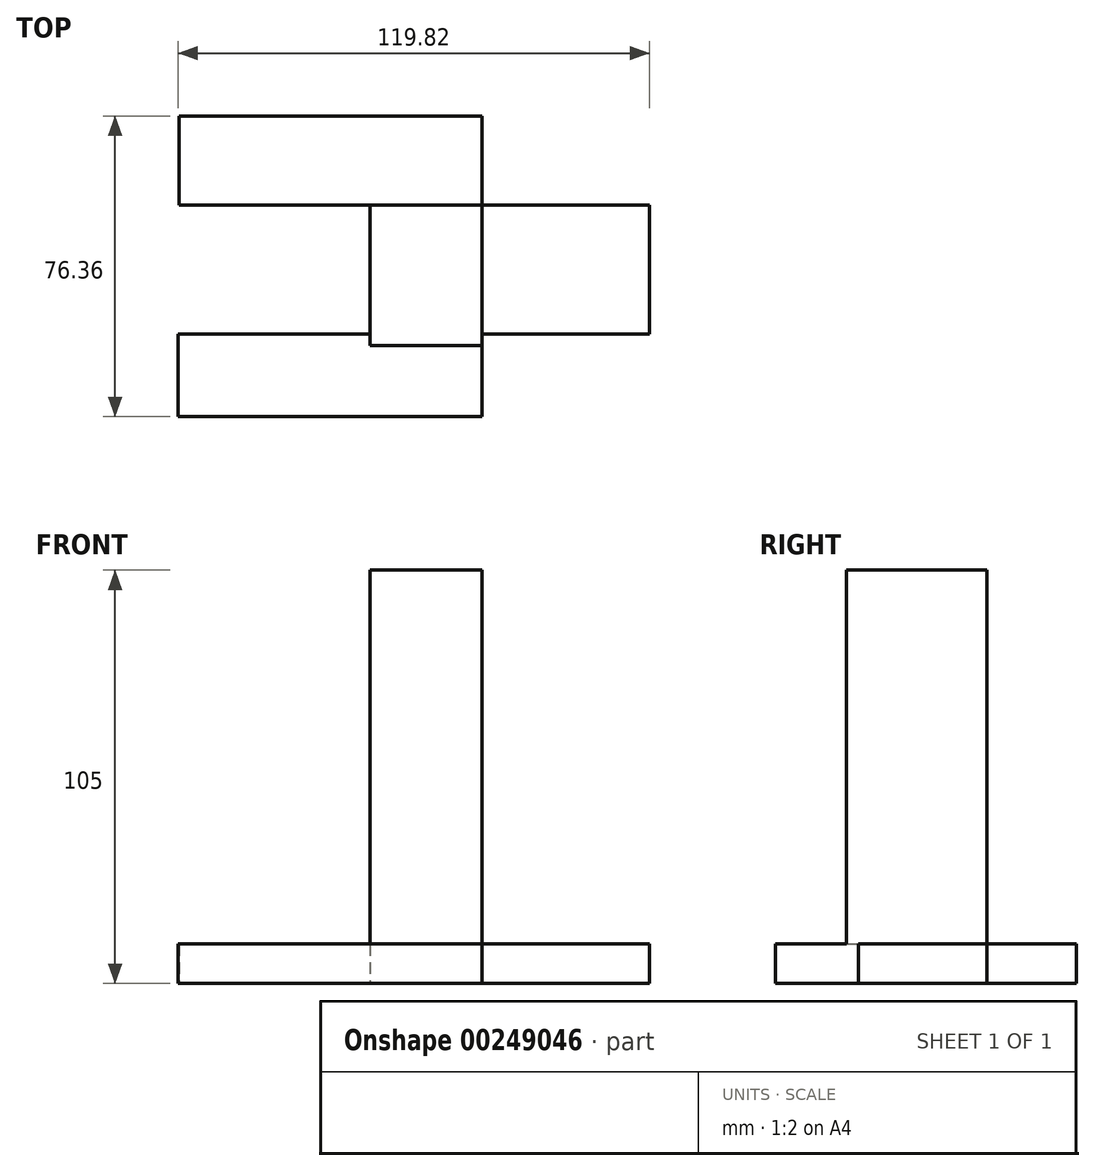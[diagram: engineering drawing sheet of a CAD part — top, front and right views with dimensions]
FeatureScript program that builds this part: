
annotation { "Feature Type Name" : "Feature", "Feature Type Description" : "" }
export const myFeature = defineFeature(function(context is Context, id is Id, definition is map)
    precondition{}
    {
        {
            var Q0;
            Q0=qCreatedBy(makeId("Top.planeOp"),FACE);
            var sketch = newSketch(context, id + "F0", { "sketchPlane" : qUnion([Q0])});
            skLineSegment(sketch, "E0", {"start": v(-59.64, 36.02) * mm, "end": v(17.27, 36.02) * mm});
            skLineSegment(sketch, "E1", {"start": v(17.27, 36.02) * mm, "end": v(17.27, 13.36) * mm});
            skLineSegment(sketch, "E2", {"start": v(17.27, 13.36) * mm, "end": v(59.9, 13.36) * mm});
            skLineSegment(sketch, "E3", {"start": v(59.9, 13.36) * mm, "end": v(59.9, -19.3) * mm});
            skLineSegment(sketch, "E4", {"start": v(59.9, -19.3) * mm, "end": v(17.27, -19.3) * mm});
            skLineSegment(sketch, "E5", {"start": v(17.27, -19.3) * mm, "end": v(17.27, -40.34) * mm});
            skLineSegment(sketch, "E6", {"start": v(17.27, -40.34) * mm, "end": v(-59.9, -40.34) * mm});
            skLineSegment(sketch, "E7", {"start": v(-59.9, -40.34) * mm, "end": v(-59.9, -19.3) * mm});
            skLineSegment(sketch, "E8", {"start": v(-59.9, -19.3) * mm, "end": v(-26.18, -19.3) * mm});
            skLineSegment(sketch, "E9", {"start": v(-26.18, -19.3) * mm, "end": v(-26.18, 13.36) * mm});
            skLineSegment(sketch, "E10", {"start": v(-26.18, 13.36) * mm, "end": v(-59.64, 13.36) * mm});
            skLineSegment(sketch, "E11", {"start": v(-59.64, 13.36) * mm, "end": v(-59.64, 36.02) * mm});
            skSolve(sketch);
        }
        {
            var Q0;
            Q0=makeQuery(id+"F0.imprint","IMPRINT",FACE,{"disambiguationData":[TD([[makeQuery(id+"F0.imprint","IMPRINT",EDGE,{"derivedFrom":sQuery(id+"F0.wireOp",EDGE,"E0")}),-1.0]])]});
            extrude(context, id + "F1", {"entities" : qUnion([Q0]), "depth" : 10 * mm});
        }
        {
            var Q0;
            Q0=makeQuery(id+"F1.opExtrude","SWEPT_FACE",FACE,{"disambiguationData":[OSD([sQuery(id+"F0.wireOp",EDGE,"E9")])]});
            extrude(context, id + "F2", {"entities" : qUnion([Q0]), "operationType" : NewBodyOperationType.REMOVE, "oppositeDirection" : true, "depth" : 15 * mm});
        }
        {
            var Q0;
            Q0=makeQuery(id+"F1.opExtrude","CAP_FACE",FACE,{"disambiguationData":[OSD([sQuery(id+"F0.wireOp",EDGE,"E0"),sQuery(id+"F0.wireOp",EDGE,"E1"),sQuery(id+"F0.wireOp",EDGE,"E2"),sQuery(id+"F0.wireOp",EDGE,"E3"),sQuery(id+"F0.wireOp",EDGE,"E4"),sQuery(id+"F0.wireOp",EDGE,"E5"),sQuery(id+"F0.wireOp",EDGE,"E6"),sQuery(id+"F0.wireOp",EDGE,"E7"),sQuery(id+"F0.wireOp",EDGE,"E8"),sQuery(id+"F0.wireOp",EDGE,"E9"),sQuery(id+"F0.wireOp",EDGE,"E10"),sQuery(id+"F0.wireOp",EDGE,"E11")])],"isStart":false});
            var sketch = newSketch(context, id + "F3", { "sketchPlane" : qUnion([Q0])});
            skLineSegment(sketch, "E12.bottom", {"start": v(-11.18, 13.36) * mm, "end": v(17.27, 13.36) * mm});
            skLineSegment(sketch, "E12.top", {"start": v(-11.18, -19.3) * mm, "end": v(17.27, -19.3) * mm});
            skLineSegment(sketch, "E12.left", {"start": v(-11.18, 13.36) * mm, "end": v(-11.18, -19.3) * mm});
            skLineSegment(sketch, "E12.right", {"start": v(17.27, 13.36) * mm, "end": v(17.27, -19.3) * mm});
            skSolve(sketch);
        }
        {
            var Q0;
            Q0=makeQuery(id+"F3.imprint","IMPRINT",FACE,{"disambiguationData":[TD([[makeQuery(id+"F3.imprint","IMPRINT",EDGE,{"derivedFrom":sQuery(id+"F3.wireOp",EDGE,"E12.bottom")}),-1.0]])]});
            extrude(context, id + "F4", {"entities" : qUnion([Q0]), "operationType" : NewBodyOperationType.ADD, "depth" : 50 * mm});
        }
        {
            var Q0;
            Q0=makeQuery(id+"F4.opExtrude","CAP_FACE",FACE,{"disambiguationData":[OSD([sQuery(id+"F3.wireOp",EDGE,"E12.bottom"),sQuery(id+"F3.wireOp",EDGE,"E12.top"),sQuery(id+"F3.wireOp",EDGE,"E12.left"),sQuery(id+"F3.wireOp",EDGE,"E12.right")])],"isStart":false});
            extrude(context, id + "F5", {"entities" : qUnion([Q0]), "operationType" : NewBodyOperationType.ADD, "depth" : 45 * mm});
        }
        {
            var Q0;
            {var subQ0=sQuery(id+"F3.wireOp",EDGE,"E12.top");Q0=makeQuery(id+"F5.boolean.opBoolean","MERGE",FACE,{"derivedFrom":[makeQuery(id+"F4.opExtrude","SWEPT_FACE",FACE,{"disambiguationData":[OSD([subQ0])]}),makeQuery(id+"F5.opExtrude","SWEPT_FACE",FACE,{"disambiguationData":[OSD([subQ0])]})]});}
            extrude(context, id + "F6", {"entities" : qUnion([Q0]), "operationType" : NewBodyOperationType.ADD, "depth" : 3 * mm});
        }
    });
